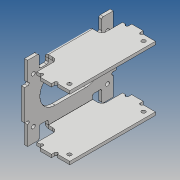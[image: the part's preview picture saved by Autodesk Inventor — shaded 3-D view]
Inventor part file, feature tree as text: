
AUTODESK INVENTOR PART (.ipt)
format: ipt  version: 2017 (Build 210142000, 142)  size: 367,616 bytes
history: native  units: mm
features: other x4, sketch x1, extrude x1
ambient origin geometry x8: Origin, YZ Plane, XZ Plane, XY Plane, X Axis, Y Axis, Z Axis, Center Point
bodies: Body1 (feature_tree)
feature tree (6):
  other  "Sólido1"
  sketch  "Boceto1"  dims[d0=4.0mm d1=40.0mm d2=2.0mm d5=2.0mm d9=15.0mm d10=20.0mm d11=75.8mm d13=120.0mm d14=58.0mm d15=23.0mm d16=4.0mm d17=4.0mm d18=0.0mm d19=4.0mm d20=2.0mm d21=8.0mm d22=4.0mm d23=90.0deg d24=0.1mm d25=4.0mm d26=2.0mm d27=8.0mm d28=4.0mm d29=90.0deg d30=0.1mm d31=8.0mm d32=7.5mm d33=15.0mm d34=5.0mm d35=10.0mm d36=7.5mm d37=40.0mm d38=20.0mm d39=12.0mm d40=4.0mm d41=6.0mm d42=2.0mm d43=6.0mm]
  extrude  "Extrusión1"  Depth=40.0mm
  other  "Pliegue1"
  other  "Pliegue2"
  other  "Definición1"
